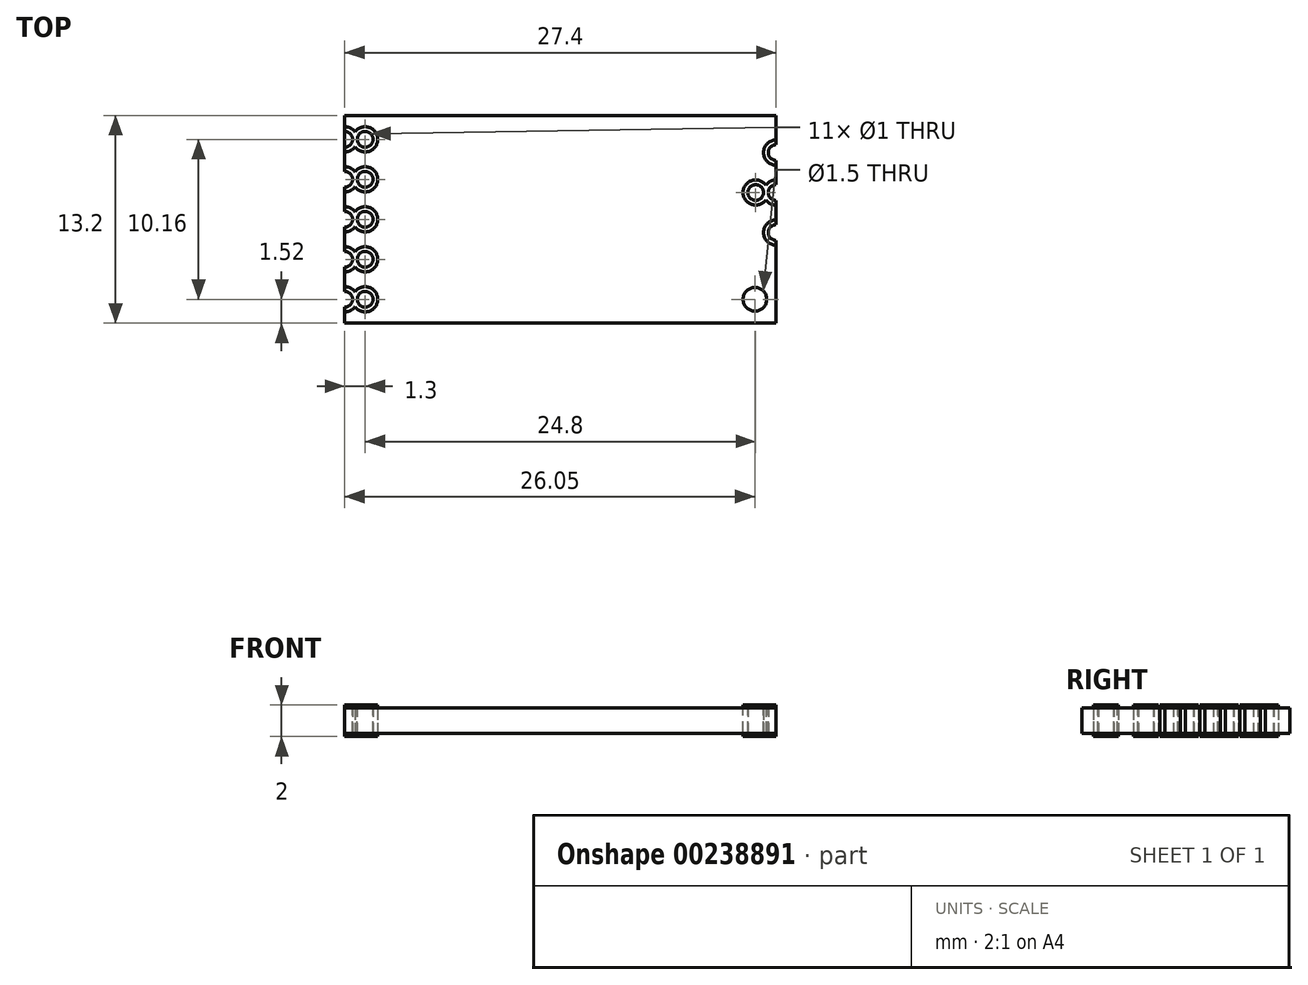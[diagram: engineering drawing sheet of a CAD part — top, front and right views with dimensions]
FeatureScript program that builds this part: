
annotation { "Feature Type Name" : "Feature", "Feature Type Description" : "" }
export const myFeature = defineFeature(function(context is Context, id is Id, definition is map)
    precondition{}
    {
        {
            var Q0;
            Q0=qCreatedBy(makeId("Top.planeOp"),FACE);
            var sketch = newSketch(context, id + "F0", { "sketchPlane" : qUnion([Q0])});
            skLineSegment(sketch, "E0.bottom", {"start": v(13.7, 6.6) * mm, "end": v(-13.7, 6.6) * mm});
            skLineSegment(sketch, "E0.top", {"start": v(13.7, -6.6) * mm, "end": v(-13.7, -6.6) * mm});
            skPoint(sketch, "E0.middle", {"position": v(0, 0) * mm});
            skCircle(sketch, "E1", {"center": v(12.35, -5.08) * mm, "radius": 0.75 * mm});
            skLineSegment(sketch, "E2", {"start": v(-13.7, 6.6) * mm, "end": v(-13.7, -6.6) * mm});
            skLineSegment(sketch, "E3", {"start": v(13.7, 6.6) * mm, "end": v(13.7, -6.6) * mm});
            skSolve(sketch);
        }
        {
            var Q0;
            {var subQ1=sQuery(id+"F0.wireOp",EDGE,"b7597baf-7a95-45c0-9827-e4552e046138.2.0.0");Q0=makeQuery(id+"F0.imprint","IMPRINT",FACE,{"disambiguationData":[TD([[makeQuery(id+"F0.imprint","IMPRINT",EDGE,{"derivedFrom":subQ1}),-1.0]])]});}
            var Q1;
            {var subQ1=sQuery(id+"F0.wireOp",EDGE,"FCyxvRw0-P2Zj-xkzr-gnyf-t4isD0P5BSW1");Q1=makeQuery(id+"F0.imprint","IMPRINT",FACE,{"disambiguationData":[TD([[makeQuery(id+"F0.imprint","IMPRINT",EDGE,{"derivedFrom":subQ1}),-1.0]])]});}
            var Q2;
            {var subQ1=sQuery(id+"F0.wireOp",EDGE,"b7597baf-7a95-45c0-9827-e4552e046138.3.0.0");Q2=makeQuery(id+"F0.imprint","IMPRINT",FACE,{"disambiguationData":[TD([[makeQuery(id+"F0.imprint","IMPRINT",EDGE,{"derivedFrom":subQ1}),-1.0]])]});}
            var Q3;
            {var subQ0=sQuery(id+"F0.wireOp",EDGE,"b7597baf-7a95-45c0-9827-e4552e046138.1.0.0");Q3=makeQuery(id+"F0.imprint","IMPRINT",FACE,{"disambiguationData":[TD([[makeQuery(id+"F0.imprint","IMPRINT",EDGE,{"derivedFrom":subQ0}),-1.0]])]});}
            var Q4;
            Q4=makeQuery(id+"F0.imprint","IMPRINT",FACE,{"disambiguationData":[TD([[makeQuery(id+"F0.imprint","IMPRINT",EDGE,{"derivedFrom":sQuery(id+"F0.wireOp",EDGE,"E1")}),1.0]])]});
            var Q5;
            {var subQ10=sQuery(id+"F0.wireOp",EDGE,"E0.bottom");Q5=makeQuery(id+"F0.imprint","IMPRINT",FACE,{"disambiguationData":[TD([[makeQuery(id+"F0.imprint","IMPRINT",EDGE,{"derivedFrom":subQ10}),1.0]])]});}
            var Q6;
            {var subQ1=sQuery(id+"F0.wireOp",EDGE,"b7597baf-7a95-45c0-9827-e4552e046138.4.0.0");Q6=makeQuery(id+"F0.imprint","IMPRINT",FACE,{"disambiguationData":[TD([[makeQuery(id+"F0.imprint","IMPRINT",EDGE,{"derivedFrom":subQ1}),-1.0]])]});}
            var Q7;
            {var subQ1=sQuery(id+"F0.wireOp",EDGE,"9d6eb106-dcc7-4875-89f1-88c796f1f74b.1.0.0");Q7=makeQuery(id+"F0.imprint","IMPRINT",FACE,{"disambiguationData":[TD([[makeQuery(id+"F0.imprint","IMPRINT",EDGE,{"derivedFrom":subQ1}),-1.0]])]});}
            var Q8;
            Q8=makeQuery(id+"F0.imprint","IMPRINT",FACE,{"disambiguationData":[TD([[makeQuery(id+"F0.imprint","IMPRINT",EDGE,{"derivedFrom":sQuery(id+"F0.wireOp",EDGE,"AzJJy44W-jtQJ-65Wj-t7PX-XcnUleVS5K7l")}),1.0]])]});
            var Q9;
            Q9=makeQuery(id+"F0.imprint","IMPRINT",FACE,{"disambiguationData":[TD([[makeQuery(id+"F0.imprint","IMPRINT",EDGE,{"derivedFrom":sQuery(id+"F0.wireOp",EDGE,"b7597baf-7a95-45c0-9827-e4552e046138.4.0.3")}),1.0]])]});
            var Q10;
            {var subQ0=sQuery(id+"F0.wireOp",EDGE,"9d6eb106-dcc7-4875-89f1-88c796f1f74b.2.0.0");Q10=makeQuery(id+"F0.imprint","IMPRINT",FACE,{"disambiguationData":[TD([[makeQuery(id+"F0.imprint","IMPRINT",EDGE,{"derivedFrom":subQ0}),-1.0]])]});}
            var Q11;
            Q11=makeQuery(id+"F0.imprint","IMPRINT",FACE,{"disambiguationData":[TD([[makeQuery(id+"F0.imprint","IMPRINT",EDGE,{"derivedFrom":sQuery(id+"F0.wireOp",EDGE,"b7597baf-7a95-45c0-9827-e4552e046138.3.0.3")}),1.0]])]});
            var Q12;
            Q12=makeQuery(id+"F0.imprint","IMPRINT",FACE,{"disambiguationData":[TD([[makeQuery(id+"F0.imprint","IMPRINT",EDGE,{"derivedFrom":sQuery(id+"F0.wireOp",EDGE,"b7597baf-7a95-45c0-9827-e4552e046138.2.0.3")}),1.0]])]});
            var Q13;
            Q13=makeQuery(id+"F0.imprint","IMPRINT",FACE,{"disambiguationData":[TD([[makeQuery(id+"F0.imprint","IMPRINT",EDGE,{"derivedFrom":sQuery(id+"F0.wireOp",EDGE,"b7597baf-7a95-45c0-9827-e4552e046138.1.0.3")}),1.0]])]});
            var Q14;
            Q14=makeQuery(id+"F0.imprint","IMPRINT",FACE,{"disambiguationData":[TD([[makeQuery(id+"F0.imprint","IMPRINT",EDGE,{"derivedFrom":sQuery(id+"F0.wireOp",EDGE,"rvVrJQ2B-IimG-XclP-EegY-UVOBJox8YtPT")}),1.0]])]});
            var Q15;
            {var subQ0=sQuery(id+"F0.wireOp",EDGE,"iEPikYkO-9StZ-AZc9-aGqD-ZBRUVysy1lso");Q15=makeQuery(id+"F0.imprint","IMPRINT",FACE,{"disambiguationData":[TD([[makeQuery(id+"F0.imprint","IMPRINT",EDGE,{"derivedFrom":subQ0}),-1.0]])]});}
            extrude(context, id + "F1", {"entities" : qUnion([Q0, Q1, Q2, Q3, Q4, Q5, Q6, Q7, Q8, Q9, Q10, Q11, Q12, Q13, Q14, Q15]), "oppositeDirection" : true, "depth" : 1.6 * mm});
        }
        {
            var Q0;
            Q0=makeQuery(id+"F0.imprint","IMPRINT",FACE,{"disambiguationData":[TD([[makeQuery(id+"F0.imprint","IMPRINT",EDGE,{"derivedFrom":sQuery(id+"F0.wireOp",EDGE,"AzJJy44W-jtQJ-65Wj-t7PX-XcnUleVS5K7l")}),1.0]])]});
            var Q1;
            Q1=makeQuery(id+"F0.imprint","IMPRINT",FACE,{"disambiguationData":[TD([[makeQuery(id+"F0.imprint","IMPRINT",EDGE,{"derivedFrom":sQuery(id+"F0.wireOp",EDGE,"E1")}),1.0]])]});
            var Q2;
            Q2=makeQuery(id+"F0.imprint","IMPRINT",FACE,{"disambiguationData":[TD([[makeQuery(id+"F0.imprint","IMPRINT",EDGE,{"derivedFrom":sQuery(id+"F0.wireOp",EDGE,"rvVrJQ2B-IimG-XclP-EegY-UVOBJox8YtPT")}),1.0]])]});
            var Q3;
            Q3=makeQuery(id+"F0.imprint","IMPRINT",FACE,{"disambiguationData":[TD([[makeQuery(id+"F0.imprint","IMPRINT",EDGE,{"derivedFrom":sQuery(id+"F0.wireOp",EDGE,"b7597baf-7a95-45c0-9827-e4552e046138.1.0.3")}),1.0]])]});
            var Q4;
            Q4=makeQuery(id+"F0.imprint","IMPRINT",FACE,{"disambiguationData":[TD([[makeQuery(id+"F0.imprint","IMPRINT",EDGE,{"derivedFrom":sQuery(id+"F0.wireOp",EDGE,"b7597baf-7a95-45c0-9827-e4552e046138.2.0.3")}),1.0]])]});
            var Q5;
            Q5=makeQuery(id+"F0.imprint","IMPRINT",FACE,{"disambiguationData":[TD([[makeQuery(id+"F0.imprint","IMPRINT",EDGE,{"derivedFrom":sQuery(id+"F0.wireOp",EDGE,"b7597baf-7a95-45c0-9827-e4552e046138.3.0.3")}),1.0]])]});
            var Q6;
            Q6=makeQuery(id+"F0.imprint","IMPRINT",FACE,{"disambiguationData":[TD([[makeQuery(id+"F0.imprint","IMPRINT",EDGE,{"derivedFrom":sQuery(id+"F0.wireOp",EDGE,"b7597baf-7a95-45c0-9827-e4552e046138.4.0.3")}),1.0]])]});
            var Q7;
            Q7=sQuery(id+"F0.wireOp",EDGE,"AzJJy44W-jtQJ-65Wj-t7PX-XcnUleVS5K7l");
            extrude(context, id + "F2", {"entities" : qUnion([Q0, Q1, Q2, Q3, Q4, Q5, Q6]), "operationType" : NewBodyOperationType.REMOVE, "surfaceEntities" : qUnion([Q7]), "endBound" : BoundingType.THROUGH_ALL, "oppositeDirection" : true, "depth" : 25 * mm});
        }
        {
            var Q0;
            Q0=makeQuery(id+"F0.imprint","IMPRINT",FACE,{"disambiguationData":[TD([[makeQuery(id+"F0.imprint","IMPRINT",EDGE,{"derivedFrom":sQuery(id+"F0.wireOp",EDGE,"E0.bottom")}),1.0]])]});
            var sketch = newSketch(context, id + "F3", { "sketchPlane" : qUnion([Q0])});
            skLineSegment(sketch, "E4.bottom", {"start": v(13.7, 6.6) * mm, "end": v(-13.7, 6.6) * mm, "construction": true});
            skLineSegment(sketch, "E4.top", {"start": v(13.7, -6.6) * mm, "end": v(-13.7, -6.6) * mm, "construction": true});
            skLineSegment(sketch, "E4.left", {"start": v(13.7, 6.6) * mm, "end": v(13.7, 4.74) * mm, "construction": true});
            skPoint(sketch, "E4.middle", {"position": v(0, 0) * mm});
            skArc(sketch, "E5", {"start": v(13.7, 4.74) * mm, "mid": v(13.2, 4.24) * mm, "end": v(13.7, 3.74) * mm});
            skLineSegment(sketch, "E6", {"start": v(-13.7, 6.6) * mm, "end": v(-13.7, 5.58) * mm, "construction": true});
            skArc(sketch, "E7", {"start": v(-13.7, 4.58) * mm, "mid": v(-13.2, 5.08) * mm, "end": v(-13.7, 5.58) * mm});
            skCircle(sketch, "E8", {"center": v(-12.4, 5.08) * mm, "radius": 0.5 * mm});
            skArc(sketch, "E9", {"start": v(-13.7, 4.28) * mm, "mid": v(-13.33, 4.37) * mm, "end": v(-13.05, 4.61) * mm});
            skArc(sketch, "E10", {"start": v(-13.05, 4.61) * mm, "mid": v(-11.6, 5.08) * mm, "end": v(-13.05, 5.55) * mm});
            skLineSegment(sketch, "E11.trimOffspring", {"start": v(-13.7, 4.58) * mm, "end": v(-13.7, 3.04) * mm});
            skArc(sketch, "E12.trimOffspring", {"start": v(-13.05, 5.55) * mm, "mid": v(-13.33, 5.8) * mm, "end": v(-13.7, 5.88) * mm});
            skArc(sketch, "E13.1.0.0", {"start": v(-13.7, 2.04) * mm, "mid": v(-13.2, 2.54) * mm, "end": v(-13.7, 3.04) * mm});
            skArc(sketch, "E13.1.0.1", {"start": v(-13.05, 3) * mm, "mid": v(-13.33, 3.25) * mm, "end": v(-13.7, 3.34) * mm});
            skArc(sketch, "E13.1.0.2", {"start": v(-13.05, 2.07) * mm, "mid": v(-11.6, 2.54) * mm, "end": v(-13.05, 3) * mm});
            skCircle(sketch, "E13.1.0.3", {"center": v(-12.4, 2.54) * mm, "radius": 0.5 * mm});
            skArc(sketch, "E13.1.0.4", {"start": v(-13.7, 1.74) * mm, "mid": v(-13.33, 1.83) * mm, "end": v(-13.05, 2.07) * mm});
            skArc(sketch, "E13.2.0.0", {"start": v(-13.7, -0.5) * mm, "mid": v(-13.2, 0) * mm, "end": v(-13.7, 0.5) * mm});
            skArc(sketch, "E13.2.0.1", {"start": v(-13.05, 0.47) * mm, "mid": v(-13.33, 0.71) * mm, "end": v(-13.7, 0.8) * mm});
            skArc(sketch, "E13.2.0.2", {"start": v(-13.05, -0.47) * mm, "mid": v(-11.6, 0) * mm, "end": v(-13.05, 0.47) * mm});
            skCircle(sketch, "E13.2.0.3", {"center": v(-12.4, 0) * mm, "radius": 0.5 * mm});
            skArc(sketch, "E13.2.0.4", {"start": v(-13.7, -0.8) * mm, "mid": v(-13.33, -0.71) * mm, "end": v(-13.05, -0.47) * mm});
            skArc(sketch, "E13.3.0.0", {"start": v(-13.7, -3.04) * mm, "mid": v(-13.2, -2.54) * mm, "end": v(-13.7, -2.04) * mm});
            skArc(sketch, "E13.3.0.1", {"start": v(-13.05, -2.07) * mm, "mid": v(-13.33, -1.83) * mm, "end": v(-13.7, -1.74) * mm});
            skArc(sketch, "E13.3.0.2", {"start": v(-13.05, -3) * mm, "mid": v(-11.6, -2.54) * mm, "end": v(-13.05, -2.07) * mm});
            skCircle(sketch, "E13.3.0.3", {"center": v(-12.4, -2.54) * mm, "radius": 0.5 * mm});
            skArc(sketch, "E13.3.0.4", {"start": v(-13.7, -3.34) * mm, "mid": v(-13.33, -3.25) * mm, "end": v(-13.05, -3) * mm});
            skArc(sketch, "E13.4.0.0", {"start": v(-13.7, -5.58) * mm, "mid": v(-13.2, -5.08) * mm, "end": v(-13.7, -4.58) * mm});
            skArc(sketch, "E13.4.0.1", {"start": v(-13.05, -4.61) * mm, "mid": v(-13.33, -4.37) * mm, "end": v(-13.7, -4.28) * mm});
            skArc(sketch, "E13.4.0.2", {"start": v(-13.05, -5.55) * mm, "mid": v(-11.6, -5.08) * mm, "end": v(-13.05, -4.61) * mm});
            skCircle(sketch, "E13.4.0.3", {"center": v(-12.4, -5.08) * mm, "radius": 0.5 * mm});
            skArc(sketch, "E13.4.0.4", {"start": v(-13.7, -5.88) * mm, "mid": v(-13.33, -5.8) * mm, "end": v(-13.05, -5.55) * mm});
            skLineSegment(sketch, "E13.direction1", {"start": v(-13.7, 4.58) * mm, "end": v(-13.7, 3.34) * mm, "construction": true});
            skLineSegment(sketch, "E14.trimOffspring", {"start": v(-13.7, 2.04) * mm, "end": v(-13.7, 0.5) * mm, "construction": true});
            skLineSegment(sketch, "E15.trimOffspring", {"start": v(-13.7, -0.5) * mm, "end": v(-13.7, -2.04) * mm, "construction": true});
            skLineSegment(sketch, "E16.trimOffspring", {"start": v(-13.7, -3.04) * mm, "end": v(-13.7, -4.58) * mm, "construction": true});
            skLineSegment(sketch, "E17.trimOffspring", {"start": v(-13.7, -5.58) * mm, "end": v(-13.7, -6.6) * mm, "construction": true});
            skArc(sketch, "E18", {"start": v(13.7, 5.04) * mm, "mid": v(12.9, 4.24) * mm, "end": v(13.7, 3.44) * mm});
            skLineSegment(sketch, "E19.trimOffspring", {"start": v(13.7, 3.74) * mm, "end": v(13.7, 2.2) * mm});
            skArc(sketch, "E20.1.0.0", {"start": v(13.7, 2.2) * mm, "mid": v(13.2, 1.7) * mm, "end": v(13.7, 1.2) * mm});
            skArc(sketch, "E20.1.0.1", {"start": v(13.7, 2.5) * mm, "mid": v(13.33, 2.41) * mm, "end": v(13.05, 2.17) * mm});
            skArc(sketch, "E20.2.0.0", {"start": v(13.7, -0.34) * mm, "mid": v(13.2, -0.84) * mm, "end": v(13.7, -1.34) * mm});
            skArc(sketch, "E20.2.0.1", {"start": v(13.7, -0.04) * mm, "mid": v(12.9, -0.84) * mm, "end": v(13.7, -1.64) * mm});
            skLineSegment(sketch, "E20.direction1", {"start": v(13.7, 3.74) * mm, "end": v(13.7, 2.2) * mm, "construction": true});
            skLineSegment(sketch, "E21.trimOffspring", {"start": v(13.7, 1.2) * mm, "end": v(13.7, -0.34) * mm, "construction": true});
            skLineSegment(sketch, "E22.trimOffspring", {"start": v(13.7, -1.34) * mm, "end": v(13.7, -6.6) * mm, "construction": true});
            skArc(sketch, "E23", {"start": v(13.05, 2.17) * mm, "mid": v(11.6, 1.7) * mm, "end": v(13.05, 1.23) * mm});
            skLineSegment(sketch, "E24", {"start": v(12.4, 1.7) * mm, "end": v(13.7, 1.7) * mm, "construction": true});
            skCircle(sketch, "E25", {"center": v(12.4, 1.7) * mm, "radius": 0.5 * mm});
            skArc(sketch, "E26.trimOffspring", {"start": v(13.05, 1.23) * mm, "mid": v(13.33, 0.99) * mm, "end": v(13.7, 0.9) * mm});
            skSolve(sketch);
        }
        {
            var Q0;
            {var subQ0=sQuery(id+"F3.wireOp",EDGE,"E20.2.0.0");Q0=makeQuery(id+"F3.imprint","IMPRINT",FACE,{"disambiguationData":[TD([[makeQuery(id+"F3.imprint","IMPRINT",EDGE,{"derivedFrom":subQ0}),-1.0]])]});}
            var Q1;
            {var subQ1=sQuery(id+"F3.wireOp",EDGE,"E13.4.0.0");Q1=makeQuery(id+"F3.imprint","IMPRINT",FACE,{"disambiguationData":[TD([[makeQuery(id+"F3.imprint","IMPRINT",EDGE,{"derivedFrom":subQ1}),-1.0]])]});}
            var Q2;
            {var subQ2=sQuery(id+"F3.wireOp",EDGE,"E7");Q2=makeQuery(id+"F3.imprint","IMPRINT",FACE,{"disambiguationData":[TD([[makeQuery(id+"F3.imprint","IMPRINT",EDGE,{"derivedFrom":subQ2}),-1.0]])]});}
            var Q3;
            {var subQ1=sQuery(id+"F3.wireOp",EDGE,"E13.1.0.0");Q3=makeQuery(id+"F3.imprint","IMPRINT",FACE,{"disambiguationData":[TD([[makeQuery(id+"F3.imprint","IMPRINT",EDGE,{"derivedFrom":subQ1}),-1.0]])]});}
            var Q4;
            {var subQ1=sQuery(id+"F3.wireOp",EDGE,"E13.2.0.0");Q4=makeQuery(id+"F3.imprint","IMPRINT",FACE,{"disambiguationData":[TD([[makeQuery(id+"F3.imprint","IMPRINT",EDGE,{"derivedFrom":subQ1}),-1.0]])]});}
            var Q5;
            {var subQ0=sQuery(id+"F3.wireOp",EDGE,"E13.3.0.0");Q5=makeQuery(id+"F3.imprint","IMPRINT",FACE,{"disambiguationData":[TD([[makeQuery(id+"F3.imprint","IMPRINT",EDGE,{"derivedFrom":subQ0}),-1.0]])]});}
            var Q6;
            {var subQ0=sQuery(id+"F3.wireOp",EDGE,"E5");Q6=makeQuery(id+"F3.imprint","IMPRINT",FACE,{"disambiguationData":[TD([[makeQuery(id+"F3.imprint","IMPRINT",EDGE,{"derivedFrom":subQ0}),-1.0]])]});}
            var Q7;
            {var subQ1=sQuery(id+"F3.wireOp",EDGE,"E20.1.0.0");Q7=makeQuery(id+"F3.imprint","IMPRINT",FACE,{"disambiguationData":[TD([[makeQuery(id+"F3.imprint","IMPRINT",EDGE,{"derivedFrom":subQ1}),-1.0]])]});}
            extrude(context, id + "F4", {"entities" : qUnion([Q0, Q1, Q2, Q3, Q4, Q5, Q6, Q7]), "depth" : 0.2 * mm, "hasSecondDirection" : true, "secondDirectionOppositeDirection" : true, "secondDirectionDepth" : (1.6 + 0.2) * mm});
        }
        {
            var Q0;
            Q0=makeQuery(id+"F3.imprint","IMPRINT",FACE,{"disambiguationData":[TD([[makeQuery(id+"F3.imprint","IMPRINT",EDGE,{"derivedFrom":sQuery(id+"F3.wireOp",EDGE,"E13.1.0.3")}),1.0]])]});
            var Q1;
            {var subQ0=sQuery(id+"F3.wireOp",EDGE,"E13.1.0.0");Q1=makeQuery(id+"F3.imprint","IMPRINT",FACE,{"disambiguationData":[TD([[makeQuery(id+"F3.imprint","IMPRINT",EDGE,{"derivedFrom":subQ0}),1.0]])]});}
            var Q2;
            Q2=makeQuery(id+"F3.imprint","IMPRINT",FACE,{"disambiguationData":[TD([[makeQuery(id+"F3.imprint","IMPRINT",EDGE,{"derivedFrom":sQuery(id+"F3.wireOp",EDGE,"E13.2.0.3")}),1.0]])]});
            var Q3;
            {var subQ0=sQuery(id+"F3.wireOp",EDGE,"E13.2.0.0");Q3=makeQuery(id+"F3.imprint","IMPRINT",FACE,{"disambiguationData":[TD([[makeQuery(id+"F3.imprint","IMPRINT",EDGE,{"derivedFrom":subQ0}),1.0]])]});}
            var Q4;
            Q4=makeQuery(id+"F3.imprint","IMPRINT",FACE,{"disambiguationData":[TD([[makeQuery(id+"F3.imprint","IMPRINT",EDGE,{"derivedFrom":sQuery(id+"F3.wireOp",EDGE,"E13.3.0.3")}),1.0]])]});
            var Q5;
            {var subQ0=sQuery(id+"F3.wireOp",EDGE,"E13.3.0.0");Q5=makeQuery(id+"F3.imprint","IMPRINT",FACE,{"disambiguationData":[TD([[makeQuery(id+"F3.imprint","IMPRINT",EDGE,{"derivedFrom":subQ0}),1.0]])]});}
            var Q6;
            Q6=makeQuery(id+"F3.imprint","IMPRINT",FACE,{"disambiguationData":[TD([[makeQuery(id+"F3.imprint","IMPRINT",EDGE,{"derivedFrom":sQuery(id+"F3.wireOp",EDGE,"E13.4.0.3")}),1.0]])]});
            var Q7;
            {var subQ0=sQuery(id+"F3.wireOp",EDGE,"E13.4.0.0");Q7=makeQuery(id+"F3.imprint","IMPRINT",FACE,{"disambiguationData":[TD([[makeQuery(id+"F3.imprint","IMPRINT",EDGE,{"derivedFrom":subQ0}),1.0]])]});}
            var Q8;
            {var subQ0=sQuery(id+"F3.wireOp",EDGE,"E20.2.0.0");Q8=makeQuery(id+"F3.imprint","IMPRINT",FACE,{"disambiguationData":[TD([[makeQuery(id+"F3.imprint","IMPRINT",EDGE,{"derivedFrom":subQ0}),1.0]])]});}
            var Q9;
            {var subQ0=sQuery(id+"F3.wireOp",EDGE,"E5");Q9=makeQuery(id+"F3.imprint","IMPRINT",FACE,{"disambiguationData":[TD([[makeQuery(id+"F3.imprint","IMPRINT",EDGE,{"derivedFrom":subQ0}),1.0]])]});}
            var Q10;
            {var subQ0=sQuery(id+"F3.wireOp",EDGE,"E20.1.0.0");Q10=makeQuery(id+"F3.imprint","IMPRINT",FACE,{"disambiguationData":[TD([[makeQuery(id+"F3.imprint","IMPRINT",EDGE,{"derivedFrom":subQ0}),1.0]])]});}
            var Q11;
            Q11=makeQuery(id+"F3.imprint","IMPRINT",FACE,{"disambiguationData":[TD([[makeQuery(id+"F3.imprint","IMPRINT",EDGE,{"derivedFrom":sQuery(id+"F3.wireOp",EDGE,"E25")}),1.0]])]});
            extrude(context, id + "F5", {"entities" : qUnion([Q0, Q1, Q2, Q3, Q4, Q5, Q6, Q7, Q8, Q9, Q10, Q11]), "operationType" : NewBodyOperationType.REMOVE, "endBound" : BoundingType.THROUGH_ALL, "oppositeDirection" : true, "depth" : 25 * mm});
        }
    });
